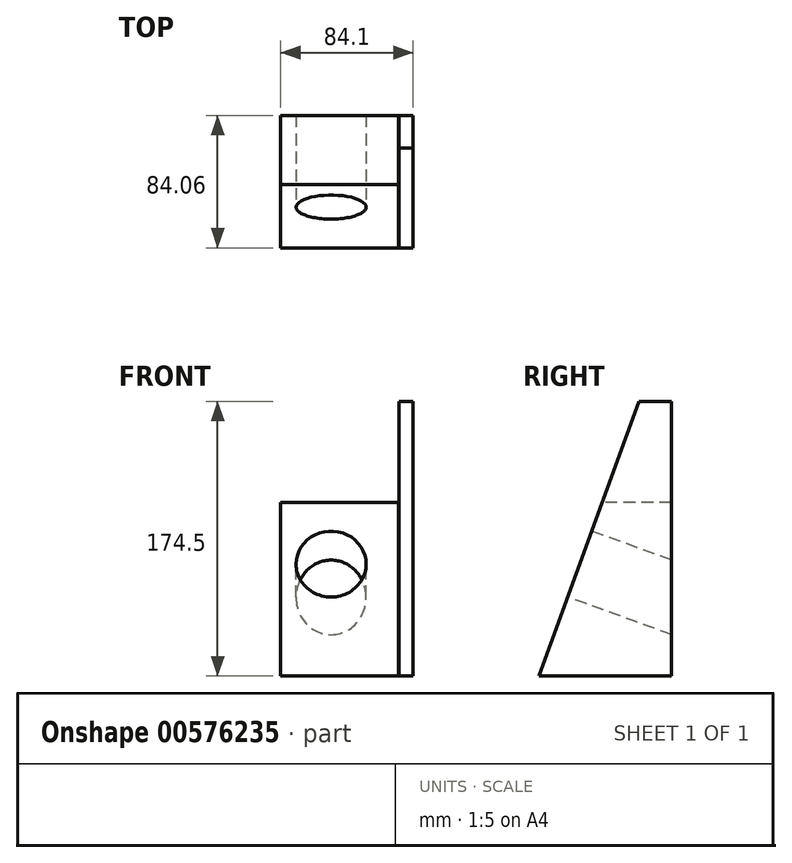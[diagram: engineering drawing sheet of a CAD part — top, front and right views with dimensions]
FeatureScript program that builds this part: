
annotation { "Feature Type Name" : "Feature", "Feature Type Description" : "" }
export const myFeature = defineFeature(function(context is Context, id is Id, definition is map)
    precondition{}
    {
        {
            var Q0;
            Q0=qCreatedBy(makeId("Top.planeOp"),FACE);
            var sketch = newSketch(context, id + "F0", { "sketchPlane" : qUnion([Q0])});
            skLineSegment(sketch, "E0.bottom", {"start": v(-30.92, 43.68) * mm, "end": v(43.17, 43.68) * mm});
            skLineSegment(sketch, "E0.top", {"start": v(-30.92, -44.09) * mm, "end": v(43.17, -44.09) * mm});
            skLineSegment(sketch, "E0.left", {"start": v(-30.92, 43.68) * mm, "end": v(-30.92, -44.09) * mm});
            skLineSegment(sketch, "E0.right", {"start": v(43.17, 43.68) * mm, "end": v(43.17, -44.09) * mm});
            skLineSegment(sketch, "E1.bottom", {"start": v(43.17, -44.09) * mm, "end": v(52.15, -44.09) * mm});
            skLineSegment(sketch, "E1.top", {"start": v(43.17, 43.88) * mm, "end": v(52.15, 43.88) * mm});
            skLineSegment(sketch, "E1.left", {"start": v(43.17, -44.09) * mm, "end": v(43.17, 43.88) * mm});
            skLineSegment(sketch, "E1.right", {"start": v(52.15, -44.09) * mm, "end": v(52.15, 43.88) * mm});
            skSolve(sketch);
        }
        {
            var Q0;
            {var subQ3=sQuery(id+"F0.wireOp",EDGE,"E1.bottom");Q0=makeQuery(id+"F0.imprint","IMPRINT",FACE,{"disambiguationData":[TD([[makeQuery(id+"F0.imprint","IMPRINT",EDGE,{"derivedFrom":subQ3}),1.0]])]});}
            extrude(context, id + "F1", {"entities" : qUnion([Q0]), "depth" : 174.5 * mm, "offsetDistance" : 25.4 * mm});
        }
        {
            var Q0;
            Q0=qCreatedBy(makeId("Top.planeOp"),FACE);
            var sketch = newSketch(context, id + "F2", { "sketchPlane" : qUnion([Q0])});
            skLineSegment(sketch, "E2.bottom", {"start": v(42.94, 43.94) * mm, "end": v(-31.95, 43.94) * mm});
            skLineSegment(sketch, "E2.top", {"start": v(42.94, -43.7) * mm, "end": v(-31.95, -43.7) * mm});
            skLineSegment(sketch, "E2.left", {"start": v(42.94, 43.94) * mm, "end": v(42.94, -43.7) * mm});
            skLineSegment(sketch, "E2.right", {"start": v(-31.95, 43.94) * mm, "end": v(-31.95, -43.7) * mm});
            skSolve(sketch);
        }
        {
            var Q0;
            Q0 = qSketchRegion(id + "F2", true);
            extrude(context, id + "F3", {"entities" : qUnion([Q0]), "depth" : 110.24 * mm, "offsetDistance" : 25.4 * mm});
        }
        {
            var Q0;
            Q0=makeQuery(id+"F3.opExtrude","CAP_FACE",FACE,{"disambiguationData":[OSD([sQuery(id+"F2.wireOp",EDGE,"E2.bottom"),sQuery(id+"F2.wireOp",EDGE,"E2.top"),sQuery(id+"F2.wireOp",EDGE,"E2.left"),sQuery(id+"F2.wireOp",EDGE,"E2.right")])],"isStart":false});
            var sketch = newSketch(context, id + "F4", { "sketchPlane" : qUnion([Q0])});
            skLineSegment(sketch, "E3", {"start": v(-31.95, 0) * mm, "end": v(42.94, 0) * mm});
            skPoint(sketch, "E3.startSnap0", {"position": v(-31.95, 0.12) * mm});
            skSolve(sketch);
        }
        {
            var Q0;
            Q0=sQuery(id+"F4.wireOp",EDGE,"E3");
            cPlane(context, id + "F5", {"entities" : qUnion([Q0]), "cplaneType" : CPlaneType.LINE_ANGLE, "offset" : 25.4 * mm, "angle" : 20 * degree, "oppositeDirection" : true, "width" : 152.4 * mm, "height" : 152.4 * mm});
        }
        {
            var Q0;
            {var subQ0=sQuery(id+"F4.wireOp",EDGE,"E3");Q0=makeQuery(id+"F4.imprint","IMPRINT",FACE,{"disambiguationData":[TD([[makeQuery(id+"F4.imprint","IMPRINT",EDGE,{"derivedFrom":subQ0}),-1.0]])]});}
            var Q1;
            Q1=qCreatedBy(id+"F5.planeOp",FACE);
            extrude(context, id + "F6", {"entities" : qUnion([Q0]), "operationType" : NewBodyOperationType.REMOVE, "endBound" : BoundingType.UP_TO_SURFACE, "oppositeDirection" : true, "depth" : 1.02 * mm, "endBoundEntityFace" : qUnion([Q1]), "offsetDistance" : 25.4 * mm});
        }
        {
            var Q0;
            Q0=makeQuery(id+"F1.opExtrude","CAP_FACE",FACE,{"disambiguationData":[OSD([sQuery(id+"F0.wireOp",EDGE,"E1.bottom"),sQuery(id+"F0.wireOp",EDGE,"E1.top"),sQuery(id+"F0.wireOp",EDGE,"E1.left"),sQuery(id+"F0.wireOp",EDGE,"E1.right")])],"isStart":false});
            var Q1;
            Q1=qCreatedBy(id+"F5.planeOp",FACE);
            extrude(context, id + "F7", {"entities" : qUnion([Q0]), "operationType" : NewBodyOperationType.REMOVE, "endBound" : BoundingType.UP_TO_SURFACE, "oppositeDirection" : true, "depth" : 25.4 * mm, "endBoundEntityFace" : qUnion([Q1]), "offsetDistance" : 25.4 * mm});
        }
        {
            var Q0;
            Q0=makeQuery(id+"F6.boolean.opBoolean","COPY",FACE,{"derivedFrom":makeQuery(id+"F6.opExtrude","CAP_FACE",FACE,{"disambiguationData":[OSD([sQuery(id+"F2.wireOp",EDGE,"E2.top"),sQuery(id+"F2.wireOp",EDGE,"E2.left"),sQuery(id+"F2.wireOp",EDGE,"E2.right"),sQuery(id+"F4.wireOp",EDGE,"E3")])],"isStart":false})});
            var sketch = newSketch(context, id + "F8", { "sketchPlane" : qUnion([Q0])});
            skCircle(sketch, "E4", {"center": v(0, 61.95) * mm, "radius": 22.26 * mm});
            skSolve(sketch);
        }
        {
            var Q0;
            Q0=makeQuery(id+"F8.imprint","IMPRINT",FACE,{"disambiguationData":[TD([[makeQuery(id+"F8.imprint","IMPRINT",EDGE,{"derivedFrom":sQuery(id+"F8.wireOp",EDGE,"E4")}),1.0]])]});
            extrude(context, id + "F9", {"entities" : qUnion([Q0]), "operationType" : NewBodyOperationType.REMOVE, "oppositeDirection" : true, "depth" : 169.93 * mm, "offsetDistance" : 25.4 * mm});
        }
    });
